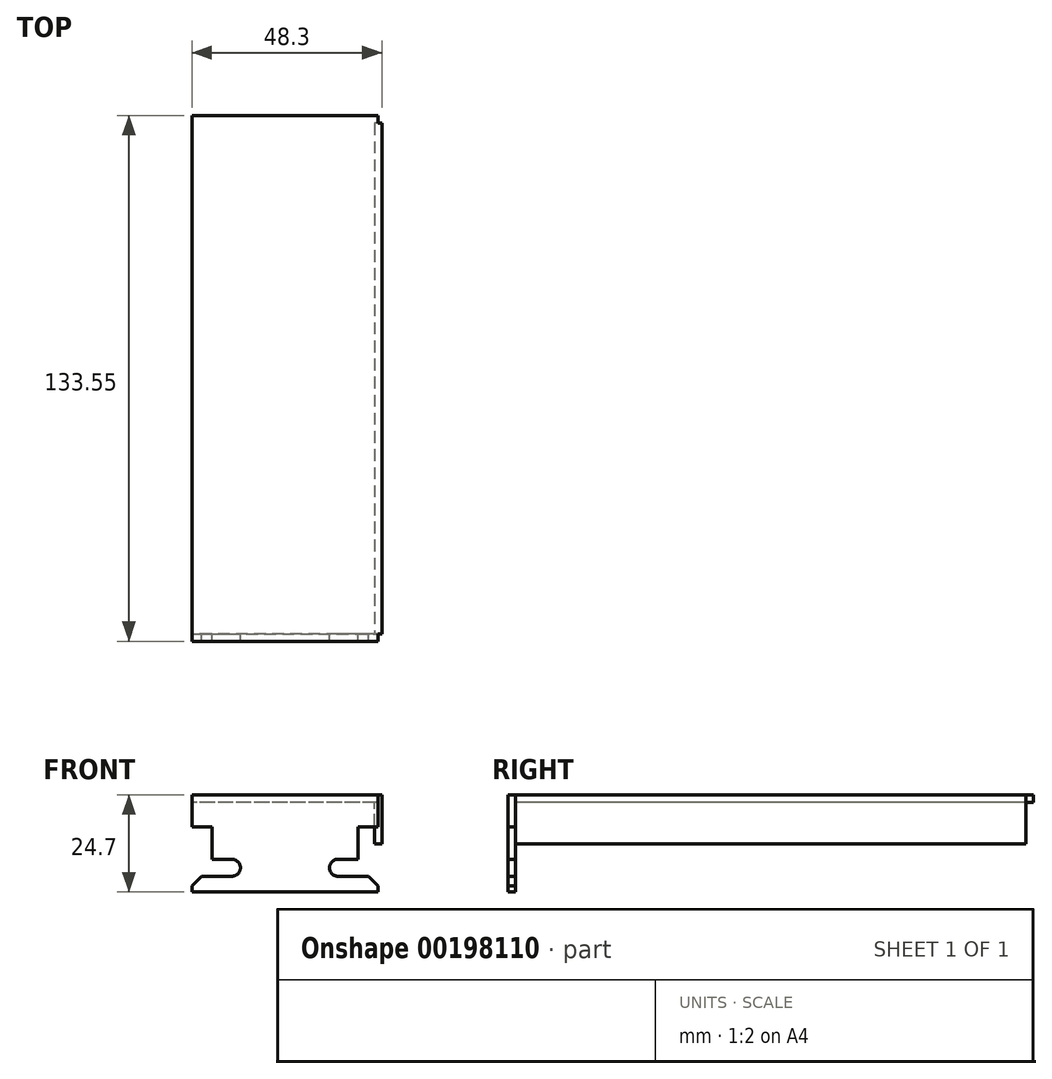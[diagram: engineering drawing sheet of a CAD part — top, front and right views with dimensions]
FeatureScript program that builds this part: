
annotation { "Feature Type Name" : "Feature", "Feature Type Description" : "" }
export const myFeature = defineFeature(function(context is Context, id is Id, definition is map)
    precondition{}
    {
        {
            var Q0;
            Q0=qCreatedBy(makeId("Front.planeOp"),FACE);
            var sketch = newSketch(context, id + "F0", { "sketchPlane" : qUnion([Q0])});
            skLineSegment(sketch, "E0.left", {"start": v(-23.65, 12.35) * mm, "end": v(-23.65, 4.15) * mm, "construction": true});
            skLineSegment(sketch, "E0.right", {"start": v(23.65, 12.35) * mm, "end": v(23.65, 4.15) * mm, "construction": true});
            skPoint(sketch, "E0.middle", {"position": v(0, 0) * mm});
            skLineSegment(sketch, "E1", {"start": v(-23.65, -10.85) * mm, "end": v(-21.18, -8.38) * mm});
            skLineSegment(sketch, "E2", {"start": v(-21.18, -8.38) * mm, "end": v(-13.48, -8.38) * mm});
            skLineSegment(sketch, "E3", {"start": v(-18.55, -4.05) * mm, "end": v(-18.55, 4.15) * mm});
            skLineSegment(sketch, "E4", {"start": v(-18.55, 4.15) * mm, "end": v(-23.65, 4.15) * mm});
            skLineSegment(sketch, "E5", {"start": v(-18.55, -4.05) * mm, "end": v(-13.48, -4.05) * mm});
            skArc(sketch, "E6", {"start": v(-13.48, -4.05) * mm, "mid": v(-11.31, -6.21) * mm, "end": v(-13.48, -8.38) * mm});
            skLineSegment(sketch, "E7", {"start": v(-23.65, 4.15) * mm, "end": v(-23.65, 12.35) * mm});
            skLineSegment(sketch, "E8.MirrorCS", {"start": v(23.65, 4.15) * mm, "end": v(23.65, 12.35) * mm});
            skLineSegment(sketch, "E9.MirrorCS", {"start": v(18.55, 4.15) * mm, "end": v(23.65, 4.15) * mm});
            skLineSegment(sketch, "E10.MirrorCS", {"start": v(18.55, -4.05) * mm, "end": v(18.55, 4.15) * mm});
            skLineSegment(sketch, "E11.MirrorCS", {"start": v(18.55, -4.05) * mm, "end": v(13.48, -4.05) * mm});
            skArc(sketch, "E12.MirrorCS", {"start": v(13.48, -4.05) * mm, "mid": v(11.31, -6.21) * mm, "end": v(13.48, -8.38) * mm});
            skLineSegment(sketch, "E13.MirrorCS", {"start": v(21.18, -8.38) * mm, "end": v(13.48, -8.38) * mm});
            skLineSegment(sketch, "E14.MirrorCS", {"start": v(23.65, -10.85) * mm, "end": v(21.18, -8.38) * mm});
            skPoint(sketch, "E15.trimOffspring.end.orphan", {"position": v(-23.65, -12.35) * mm});
            skPoint(sketch, "E16.trimOffspring.end.orphan", {"position": v(23.65, -12.35) * mm});
            skLineSegment(sketch, "E17", {"start": v(-23.65, -10.85) * mm, "end": v(-23.65, -12.35) * mm});
            skLineSegment(sketch, "E18", {"start": v(23.65, -12.35) * mm, "end": v(23.65, -10.85) * mm});
            skLineSegment(sketch, "E19", {"start": v(-23.65, -12.35) * mm, "end": v(23.65, -12.35) * mm});
            skLineSegment(sketch, "E20", {"start": v(-23.65, 12.35) * mm, "end": v(23.65, 12.35) * mm});
            skSolve(sketch);
        }
        {
            var Q0;
            Q0 = qSketchRegion(id + "F0", true);
            extrude(context, id + "F1", {"entities" : qUnion([Q0]), "depth" : 1.9 * mm});
        }
        {
            var Q0;
            Q0=makeQuery(id+"F1.opExtrude","CAP_FACE",FACE,{"disambiguationData":[OSD([sQuery(id+"F0.wireOp",EDGE,"E1"),sQuery(id+"F0.wireOp",EDGE,"E2"),sQuery(id+"F0.wireOp",EDGE,"E3"),sQuery(id+"F0.wireOp",EDGE,"E4"),sQuery(id+"F0.wireOp",EDGE,"E5"),sQuery(id+"F0.wireOp",EDGE,"E6"),sQuery(id+"F0.wireOp",EDGE,"E7"),sQuery(id+"F0.wireOp",EDGE,"E8.MirrorCS"),sQuery(id+"F0.wireOp",EDGE,"E9.MirrorCS"),sQuery(id+"F0.wireOp",EDGE,"E10.MirrorCS"),sQuery(id+"F0.wireOp",EDGE,"E11.MirrorCS"),sQuery(id+"F0.wireOp",EDGE,"E12.MirrorCS"),sQuery(id+"F0.wireOp",EDGE,"E13.MirrorCS"),sQuery(id+"F0.wireOp",EDGE,"E14.MirrorCS"),sQuery(id+"F0.wireOp",EDGE,"E17"),sQuery(id+"F0.wireOp",EDGE,"E18"),sQuery(id+"F0.wireOp",EDGE,"E19"),sQuery(id+"F0.wireOp",EDGE,"E20")])],"isStart":true});
            var sketch = newSketch(context, id + "F2", { "sketchPlane" : qUnion([Q0])});
            skLineSegment(sketch, "E21.bottom", {"start": v(-23.65, 12.35) * mm, "end": v(23.65, 12.35) * mm});
            skLineSegment(sketch, "E21.top", {"start": v(-23.65, 10.45) * mm, "end": v(23.65, 10.45) * mm});
            skLineSegment(sketch, "E21.left", {"start": v(-23.65, 12.35) * mm, "end": v(-23.65, 10.45) * mm});
            skLineSegment(sketch, "E21.right", {"start": v(23.65, 12.35) * mm, "end": v(23.65, 10.45) * mm});
            skSolve(sketch);
        }
        {
            var Q0;
            Q0 = qSketchRegion(id + "F2", true);
            extrude(context, id + "F3", {"entities" : qUnion([Q0]), "operationType" : NewBodyOperationType.ADD, "depth" : 131.65 * mm});
        }
        {
            var Q0;
            Q0=makeQuery(id+"F3.opExtrude","CAP_EDGE",EDGE,{"disambiguationData":[OSD([sQuery(id+"F2.wireOp",EDGE,"E21.bottom")])],"isStart":false});
            cPoint(context, id + "F4", {"entities" : qUnion([Q0]), "parameter" : 0.5});
        }
        {
            var Q0;
            Q0=makeQuery(id+"F1.opExtrude","CAP_EDGE",EDGE,{"disambiguationData":[OSD([sQuery(id+"F0.wireOp",EDGE,"E20")])],"isStart":false});
            cPoint(context, id + "F5", {"entities" : qUnion([Q0]), "parameter" : 0.5});
        }
        {
            var Q0;
            Q0 = qCreatedBy(id + "F4" ,VERTEX);
            var Q1;
            Q1 = qCreatedBy(id + "F5" ,VERTEX);
            cPlane(context, id + "F6", {"entities" : qUnion([Q0, Q1]), "cplaneType" : CPlaneType.MID_PLANE, "offset" : 25 * mm, "flipAlignment" : true, "width" : 150 * mm, "height" : 150 * mm});
        }
        {
            var Q0;
            Q0=makeQuery(id+"F3.boolean.opBoolean","MERGE",FACE,{"derivedFrom":[makeQuery(id+"F1.opExtrude","SWEPT_FACE",FACE,{"disambiguationData":[OSD([sQuery(id+"F0.wireOp",EDGE,"E8.MirrorCS")])]}),makeQuery(id+"F3.opExtrude","SWEPT_FACE",FACE,{"disambiguationData":[OSD([sQuery(id+"F2.wireOp",EDGE,"E21.left")])]})]});
            var sketch = newSketch(context, id + "F7", { "sketchPlane" : qUnion([Q0])});
            skLineSegment(sketch, "E22.bottom", {"start": v(0, 10.45) * mm, "end": v(129.7, 10.45) * mm});
            skLineSegment(sketch, "E22.top", {"start": v(0, 12.35) * mm, "end": v(129.7, 12.35) * mm});
            skLineSegment(sketch, "E22.left", {"start": v(0, 10.45) * mm, "end": v(0, 12.35) * mm});
            skLineSegment(sketch, "E22.right", {"start": v(129.7, 10.45) * mm, "end": v(129.7, 12.35) * mm});
            skSolve(sketch);
        }
        {
            var Q0;
            Q0 = qSketchRegion(id + "F7", true);
            extrude(context, id + "F8", {"entities" : qUnion([Q0]), "operationType" : NewBodyOperationType.ADD, "depth" : 1 * mm});
        }
        {
            var Q0;
            Q0=makeQuery(id+"F8.boolean.opBoolean","MERGE",FACE,{"derivedFrom":[makeQuery(id+"F3.opExtrude","SWEPT_FACE",FACE,{"disambiguationData":[OSD([sQuery(id+"F2.wireOp",EDGE,"E21.top")])]}),makeQuery(id+"F8.opExtrude","SWEPT_FACE",FACE,{"disambiguationData":[OSD([sQuery(id+"F7.wireOp",EDGE,"E22.bottom")])]})]});
            var sketch = newSketch(context, id + "F9", { "sketchPlane" : qUnion([Q0])});
            skLineSegment(sketch, "E23.bottom", {"start": v(24.65, -129.7) * mm, "end": v(22.75, -129.7) * mm});
            skLineSegment(sketch, "E23.top", {"start": v(24.65, 0) * mm, "end": v(22.75, 0) * mm});
            skLineSegment(sketch, "E23.left", {"start": v(24.65, -129.7) * mm, "end": v(24.65, 0) * mm});
            skLineSegment(sketch, "E23.right", {"start": v(22.75, -129.7) * mm, "end": v(22.75, 0) * mm});
            skSolve(sketch);
        }
        {
            var Q0;
            Q0 = qSketchRegion(id + "F9", true);
            extrude(context, id + "F10", {"entities" : qUnion([Q0]), "operationType" : NewBodyOperationType.ADD, "depth" : 10.6 * mm});
        }
    });
